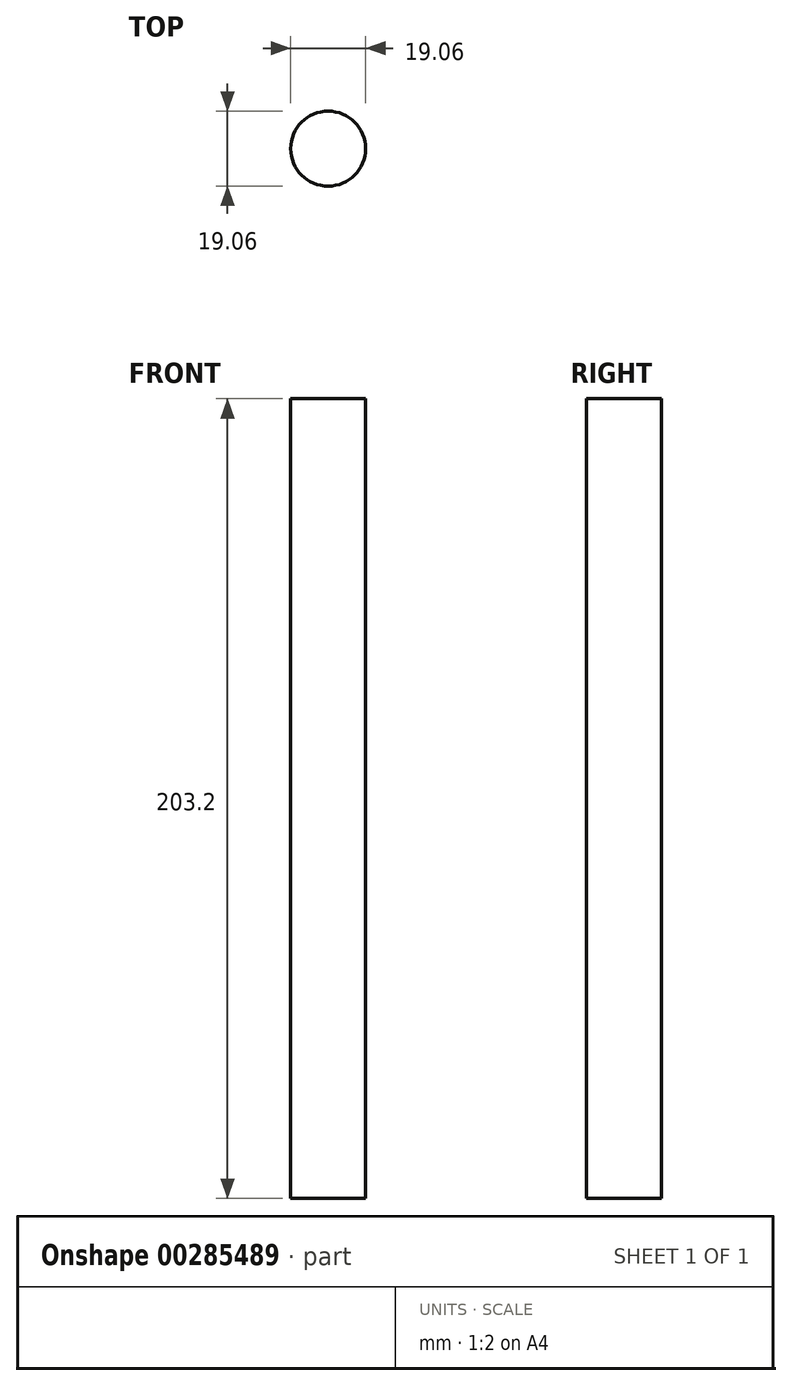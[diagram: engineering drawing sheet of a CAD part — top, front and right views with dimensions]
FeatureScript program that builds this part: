
annotation { "Feature Type Name" : "Feature", "Feature Type Description" : "" }
export const myFeature = defineFeature(function(context is Context, id is Id, definition is map)
    precondition{}
    {
        {
            var Q0;
            Q0=qCreatedBy(makeId("Top.planeOp"),FACE);
            var sketch = newSketch(context, id + "F0", { "sketchPlane" : qUnion([Q0])});
            skCircle(sketch, "E0", {"center": v(0, 0) * mm, "radius": 9.53 * mm});
            skSolve(sketch);
        }
        {
            var Q0;
            Q0 = qSketchRegion(id + "F0", true);
            extrude(context, id + "F1", {"entities" : qUnion([Q0]), "depth" : 203.2 * mm});
        }
    });
